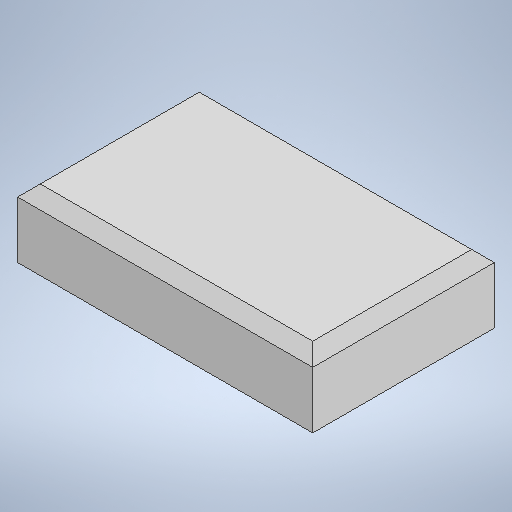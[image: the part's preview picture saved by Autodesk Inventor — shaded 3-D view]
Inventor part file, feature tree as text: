
AUTODESK INVENTOR PART (.ipt)
format: ipt  version: 2025.1 (Build 291241000, 241)  size: 217,600 bytes
history: native  units: mm
features: sketch x2, extrude x1, hole x1, chamfer x1
ambient origin geometry x8: Origin, YZ Plane, XZ Plane, XY Plane, X Axis, Y Axis, Z Axis, Center Point
bodies: Solid1 (feature_tree)
feature tree (5):
  extrude  "Extrusion1"  Depth=130.0mm
  hole  "Hole1"  [1 undecoded]
  chamfer  "Chamfer1"  [1 undecoded]
  sketch  "Sketch1"  dims[d0=80.0mm d1=130.0mm]
  sketch  "Sketch2"  dims[d2=30.0mm d3=0.0mm d4=5.0mm d5=2.0mm d6=45.0deg d8=9.0mm d9=6.0mm d10=10.0mm d11=2.0mm d12=90.0deg d13=8.0mm d14=0.0mm]
note: 2 required parameter values undecoded (feature->parameter linkage not recoverable at this tier; creation-order binding heuristic only, values carry confidence <= 0.55)
